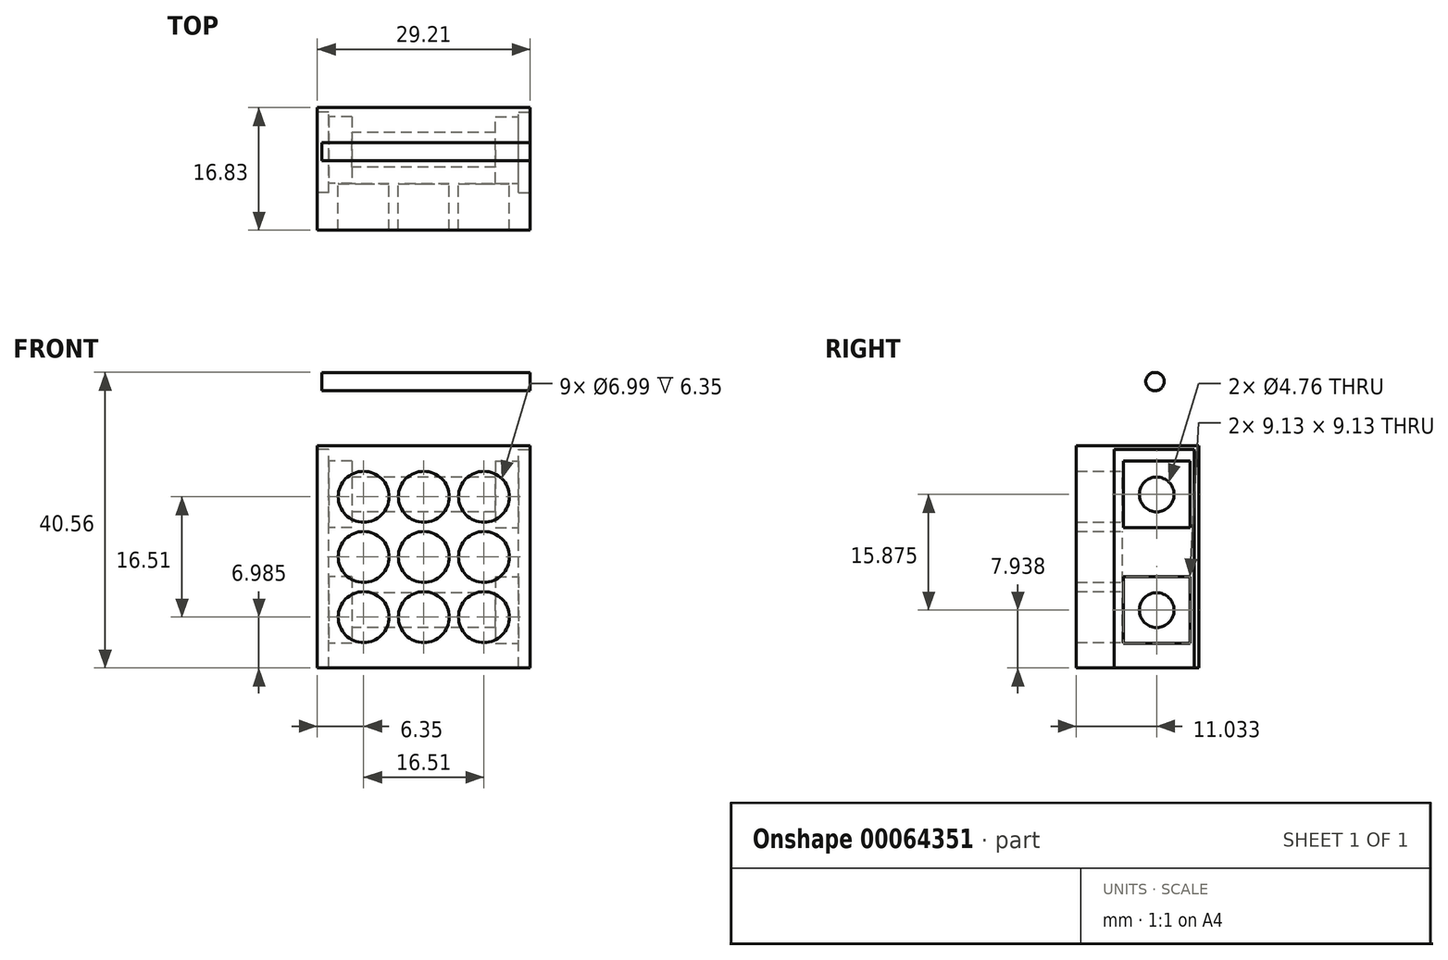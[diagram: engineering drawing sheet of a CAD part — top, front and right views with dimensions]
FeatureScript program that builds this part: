
annotation { "Feature Type Name" : "Feature", "Feature Type Description" : "" }
export const myFeature = defineFeature(function(context is Context, id is Id, definition is map)
    precondition{}
    {
        {
            var Q0;
            Q0=qCreatedBy(makeId("Front.planeOp"),FACE);
            var sketch = newSketch(context, id + "F0", { "sketchPlane" : qUnion([Q0])});
            skLineSegment(sketch, "E0.bottom", {"start": v(0, 0) * mm, "end": v(-29.2, 0) * mm});
            skLineSegment(sketch, "E0.top", {"start": v(0, 30.48) * mm, "end": v(-29.2, 30.48) * mm});
            skLineSegment(sketch, "E0.left", {"start": v(0, 0) * mm, "end": v(0, 30.48) * mm});
            skLineSegment(sketch, "E0.right", {"start": v(-29.2, 0) * mm, "end": v(-29.2, 30.48) * mm});
            skLineSegment(sketch, "E1", {"start": v(-6.35, 30.48) * mm, "end": v(-6.35, 0) * mm, "construction": true});
            skLineSegment(sketch, "E2", {"start": v(-14.6, 30.48) * mm, "end": v(-14.6, 0) * mm, "construction": true});
            skLineSegment(sketch, "E3", {"start": v(-29.2, 23.5) * mm, "end": v(0, 23.5) * mm, "construction": true});
            skLineSegment(sketch, "E4", {"start": v(0, 15.24) * mm, "end": v(-29.21, 15.24) * mm, "construction": true});
            skCircle(sketch, "E5", {"center": v(-6.35, 23.5) * mm, "radius": 3.5 * mm});
            skLineSegment(sketch, "E6", {"start": v(-22.86, 30.48) * mm, "end": v(-22.86, 0) * mm, "construction": true});
            skLineSegment(sketch, "E7", {"start": v(-29.21, 6.98) * mm, "end": v(0, 6.99) * mm, "construction": true});
            skCircle(sketch, "E8.0.1.0", {"center": v(-6.35, 15.24) * mm, "radius": 3.5 * mm});
            skCircle(sketch, "E8.0.2.0", {"center": v(-6.35, 6.98) * mm, "radius": 3.5 * mm});
            skCircle(sketch, "E8.1.0.0", {"center": v(-14.6, 23.5) * mm, "radius": 3.5 * mm});
            skCircle(sketch, "E8.1.1.0", {"center": v(-14.6, 15.24) * mm, "radius": 3.5 * mm});
            skCircle(sketch, "E8.1.2.0", {"center": v(-14.6, 6.98) * mm, "radius": 3.5 * mm});
            skCircle(sketch, "E8.2.0.0", {"center": v(-22.86, 23.5) * mm, "radius": 3.5 * mm});
            skCircle(sketch, "E8.2.1.0", {"center": v(-22.86, 15.24) * mm, "radius": 3.5 * mm});
            skCircle(sketch, "E8.2.2.0", {"center": v(-22.86, 6.98) * mm, "radius": 3.5 * mm});
            skLineSegment(sketch, "E8.direction1", {"start": v(-6.35, 23.5) * mm, "end": v(-14.6, 23.5) * mm, "construction": true});
            skLineSegment(sketch, "E8.direction2", {"start": v(-6.35, 23.5) * mm, "end": v(-6.35, 15.24) * mm, "construction": true});
            skSolve(sketch);
        }
        {
            var Q0;
            Q0=makeQuery(id+"F0.imprint","IMPRINT",FACE,{"disambiguationData":[TD([[makeQuery(id+"F0.imprint","IMPRINT",EDGE,{"derivedFrom":sQuery(id+"F0.wireOp",EDGE,"E0.bottom")}),-1.0]])]});
            extrude(context, id + "F1", {"entities" : qUnion([Q0]), "depth" : 6.35 * mm});
        }
        {
            var Q0;
            Q0=makeQuery(id+"F1.opExtrude","CAP_FACE",FACE,{"disambiguationData":[OSD([sQuery(id+"F0.wireOp",EDGE,"E0.bottom"),sQuery(id+"F0.wireOp",EDGE,"E0.top"),sQuery(id+"F0.wireOp",EDGE,"E0.left"),sQuery(id+"F0.wireOp",EDGE,"E0.right"),sQuery(id+"F0.wireOp",EDGE,"E5"),sQuery(id+"F0.wireOp",EDGE,"E8.0.1.0"),sQuery(id+"F0.wireOp",EDGE,"E8.0.2.0"),sQuery(id+"F0.wireOp",EDGE,"E8.1.0.0"),sQuery(id+"F0.wireOp",EDGE,"E8.1.1.0"),sQuery(id+"F0.wireOp",EDGE,"E8.1.2.0"),sQuery(id+"F0.wireOp",EDGE,"E8.2.0.0"),sQuery(id+"F0.wireOp",EDGE,"E8.2.1.0"),sQuery(id+"F0.wireOp",EDGE,"E8.2.2.0")])],"isStart":true});
            var sketch = newSketch(context, id + "F2", { "sketchPlane" : qUnion([Q0])});
            skLineSegment(sketch, "E9.bottom", {"start": v(0, 30.48) * mm, "end": v(29.2, 30.48) * mm});
            skLineSegment(sketch, "E9.top", {"start": v(0, 0) * mm, "end": v(29.2, 0) * mm});
            skLineSegment(sketch, "E9.left", {"start": v(0, 30.48) * mm, "end": v(0, 0) * mm});
            skLineSegment(sketch, "E9.right", {"start": v(29.2, 30.48) * mm, "end": v(29.2, 0) * mm});
            skSolve(sketch);
        }
        {
            var Q0;
            Q0=qSketchRegion(id+"F2",true);
            extrude(context, id + "F3", {"entities" : qUnion([Q0]), "operationType" : NewBodyOperationType.ADD, "depth" : 10.48 * mm});
        }
        {
            var Q0;
            Q0=makeQuery(id+"F3.boolean.opBoolean","MERGE",FACE,{"derivedFrom":[makeQuery(id+"F1.opExtrude","SWEPT_FACE",FACE,{"disambiguationData":[OSD([sQuery(id+"F0.wireOp",EDGE,"E0.left")])]}),makeQuery(id+"F3.opExtrude","SWEPT_FACE",FACE,{"disambiguationData":[OSD([sQuery(id+"F2.wireOp",EDGE,"E9.left")])]})]});
            var sketch = newSketch(context, id + "F4", { "sketchPlane" : qUnion([Q0])});
            skLineSegment(sketch, "E10.bottom", {"start": v(-1.16, 0) * mm, "end": v(9.84, 0) * mm});
            skLineSegment(sketch, "E10.top", {"start": v(-1.16, 30) * mm, "end": v(9.84, 30) * mm});
            skLineSegment(sketch, "E10.left", {"start": v(-1.16, 0) * mm, "end": v(-1.16, 30) * mm});
            skLineSegment(sketch, "E10.right", {"start": v(9.84, 0) * mm, "end": v(9.84, 30) * mm});
            skSolve(sketch);
        }
        {
            var Q0;
            Q0=qSketchRegion(id+"F4",true);
            extrude(context, id + "F5", {"entities" : qUnion([Q0]), "operationType" : NewBodyOperationType.REMOVE, "oppositeDirection" : true, "depth" : 1.59 * mm});
        }
        {
            var Q0;
            Q0=makeQuery(id+"F3.boolean.opBoolean","MERGE",FACE,{"derivedFrom":[makeQuery(id+"F1.opExtrude","SWEPT_FACE",FACE,{"disambiguationData":[OSD([sQuery(id+"F0.wireOp",EDGE,"E0.right")])]}),makeQuery(id+"F3.opExtrude","SWEPT_FACE",FACE,{"disambiguationData":[OSD([sQuery(id+"F2.wireOp",EDGE,"E9.right")])]})]});
            var sketch = newSketch(context, id + "F6", { "sketchPlane" : qUnion([Q0])});
            skLineSegment(sketch, "E11.bottom", {"start": v(-9.84, 0) * mm, "end": v(1.16, 0) * mm});
            skLineSegment(sketch, "E11.top", {"start": v(-9.84, 30) * mm, "end": v(1.16, 30) * mm});
            skLineSegment(sketch, "E11.left", {"start": v(-9.84, 0) * mm, "end": v(-9.84, 30) * mm});
            skLineSegment(sketch, "E11.right", {"start": v(1.16, 0) * mm, "end": v(1.16, 30) * mm});
            skSolve(sketch);
        }
        {
            var Q0;
            Q0=qSketchRegion(id+"F6",true);
            extrude(context, id + "F7", {"entities" : qUnion([Q0]), "operationType" : NewBodyOperationType.REMOVE, "oppositeDirection" : true, "depth" : 1.59 * mm});
        }
        {
            var Q0;
            Q0=makeQuery(id+"F7.boolean.opBoolean","COPY",FACE,{"derivedFrom":makeQuery(id+"F7.opExtrude","CAP_FACE",FACE,{"disambiguationData":[OSD([sQuery(id+"F6.wireOp",EDGE,"E11.bottom"),sQuery(id+"F6.wireOp",EDGE,"E11.top"),sQuery(id+"F6.wireOp",EDGE,"E11.left"),sQuery(id+"F6.wireOp",EDGE,"E11.right")])],"isStart":false})});
            var sketch = newSketch(context, id + "F8", { "sketchPlane" : qUnion([Q0])});
            skCircle(sketch, "E12", {"center": v(-4.68, 23.81) * mm, "radius": 2.38 * mm});
            skCircle(sketch, "E13", {"center": v(-4.68, 7.94) * mm, "radius": 2.38 * mm});
            skLineSegment(sketch, "E14", {"start": v(-4.68, 30) * mm, "end": v(-4.68, 0) * mm, "construction": true});
            skPoint(sketch, "E15", {"position": v(-4.68, 30) * mm});
            skSolve(sketch);
        }
        {
            var Q0;
            Q0=qSketchRegion(id+"F8",true);
            extrude(context, id + "F9", {"entities" : qUnion([Q0]), "operationType" : NewBodyOperationType.REMOVE, "endBound" : BoundingType.THROUGH_ALL, "oppositeDirection" : true, "depth" : 25.4 * mm});
        }
        {
            var Q0;
            Q0=makeQuery(id+"F7.boolean.opBoolean","COPY",FACE,{"derivedFrom":makeQuery(id+"F7.opExtrude","CAP_FACE",FACE,{"disambiguationData":[OSD([sQuery(id+"F6.wireOp",EDGE,"E11.bottom"),sQuery(id+"F6.wireOp",EDGE,"E11.top"),sQuery(id+"F6.wireOp",EDGE,"E11.left"),sQuery(id+"F6.wireOp",EDGE,"E11.right")])],"isStart":false})});
            var sketch = newSketch(context, id + "F10", { "sketchPlane" : qUnion([Q0])});
            skLineSegment(sketch, "E16.bottom", {"start": v(-9.25, 28.38) * mm, "end": v(-0.12, 28.38) * mm});
            skLineSegment(sketch, "E16.top", {"start": v(-9.25, 19.25) * mm, "end": v(-0.12, 19.25) * mm});
            skLineSegment(sketch, "E16.left", {"start": v(-9.25, 28.38) * mm, "end": v(-9.25, 19.25) * mm});
            skLineSegment(sketch, "E16.right", {"start": v(-0.12, 28.38) * mm, "end": v(-0.12, 19.25) * mm});
            skPoint(sketch, "E16.middle", {"position": v(-4.68, 23.81) * mm});
            skLineSegment(sketch, "E17.bottom", {"start": v(-9.25, 12.5) * mm, "end": v(-0.12, 12.5) * mm});
            skLineSegment(sketch, "E17.top", {"start": v(-9.25, 3.37) * mm, "end": v(-0.12, 3.37) * mm});
            skLineSegment(sketch, "E17.left", {"start": v(-9.25, 12.5) * mm, "end": v(-9.25, 3.37) * mm});
            skLineSegment(sketch, "E17.right", {"start": v(-0.12, 12.5) * mm, "end": v(-0.12, 3.37) * mm});
            skPoint(sketch, "E17.middle", {"position": v(-4.68, 7.94) * mm});
            skPoint(sketch, "E17.cornerSnap0", {"position": v(-9.25, 23.81) * mm});
            skSolve(sketch);
        }
        {
            var Q0;
            Q0=makeQuery(id+"F5.boolean.opBoolean","COPY",FACE,{"derivedFrom":makeQuery(id+"F5.opExtrude","CAP_FACE",FACE,{"disambiguationData":[OSD([sQuery(id+"F4.wireOp",EDGE,"E10.bottom"),sQuery(id+"F4.wireOp",EDGE,"E10.top"),sQuery(id+"F4.wireOp",EDGE,"E10.left"),sQuery(id+"F4.wireOp",EDGE,"E10.right")])],"isStart":false})});
            var sketch = newSketch(context, id + "F11", { "sketchPlane" : qUnion([Q0])});
            skLineSegment(sketch, "E18.bottom", {"start": v(0.12, 28.38) * mm, "end": v(9.25, 28.38) * mm});
            skLineSegment(sketch, "E18.top", {"start": v(0.12, 19.25) * mm, "end": v(9.25, 19.25) * mm});
            skLineSegment(sketch, "E18.left", {"start": v(0.12, 28.38) * mm, "end": v(0.12, 19.25) * mm});
            skLineSegment(sketch, "E18.right", {"start": v(9.25, 28.38) * mm, "end": v(9.25, 19.25) * mm});
            skPoint(sketch, "E18.middle", {"position": v(4.68, 23.81) * mm});
            skLineSegment(sketch, "E19.bottom", {"start": v(0.12, 12.5) * mm, "end": v(9.25, 12.5) * mm});
            skLineSegment(sketch, "E19.top", {"start": v(0.12, 3.37) * mm, "end": v(9.25, 3.37) * mm});
            skLineSegment(sketch, "E19.left", {"start": v(0.12, 12.5) * mm, "end": v(0.12, 3.37) * mm});
            skLineSegment(sketch, "E19.right", {"start": v(9.25, 12.5) * mm, "end": v(9.25, 3.37) * mm});
            skPoint(sketch, "E19.middle", {"position": v(4.68, 7.94) * mm});
            skSolve(sketch);
        }
        {
            var Q0;
            Q0=qSketchRegion(id+"F10",true);
            extrude(context, id + "F12", {"entities" : qUnion([Q0]), "operationType" : NewBodyOperationType.REMOVE, "oppositeDirection" : true, "depth" : 3.17 * mm});
        }
        {
            var Q0;
            Q0=qSketchRegion(id+"F11",true);
            extrude(context, id + "F13", {"entities" : qUnion([Q0]), "operationType" : NewBodyOperationType.REMOVE, "oppositeDirection" : true, "depth" : 3.17 * mm});
        }
        {
            var Q0;
            Q0=makeQuery(id+"F3.boolean.opBoolean","MERGE",FACE,{"derivedFrom":[makeQuery(id+"F1.opExtrude","SWEPT_FACE",FACE,{"disambiguationData":[OSD([sQuery(id+"F0.wireOp",EDGE,"E0.left")])]}),makeQuery(id+"F3.opExtrude","SWEPT_FACE",FACE,{"disambiguationData":[OSD([sQuery(id+"F2.wireOp",EDGE,"E9.left")])]})]});
            var sketch = newSketch(context, id + "F14", { "sketchPlane" : qUnion([Q0])});
            skCircle(sketch, "E20", {"center": v(4.45, 39.3) * mm, "radius": 1.26 * mm});
            skSolve(sketch);
        }
        {
            var Q0;
            Q0=qSketchRegion(id+"F14",true);
            var Q1;
            Q1=sQuery(id+"F14.wireOp",EDGE,"E20");
            extrude(context, id + "F15", {"entities" : qUnion([Q0]), "surfaceEntities" : qUnion([Q1]), "oppositeDirection" : true, "depth" : 28.57 * mm});
        }
    });
